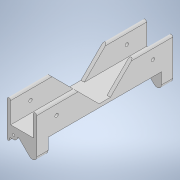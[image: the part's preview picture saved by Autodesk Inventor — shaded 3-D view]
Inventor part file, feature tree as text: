
AUTODESK INVENTOR PART (.ipt)
format: ipt  version: 2022 (Build 260153000, 153)  size: 276,480 bytes
history: native  units: mm
features: sketch x8, extrude x7, fillet x6, projected_geometry x5, plane x2, chamfer x2, mirror x1, hole x1
ambient origin geometry x8: Origin, YZ Plane, XZ Plane, XY Plane, X Axis, Y Axis, Z Axis, Center Point
bodies: Body1 (feature_tree)
feature tree (32):
  extrude  "Extrusion2"  Depth=3.0mm
  extrude  "Extrusion3"  Depth=20.0mm
  plane  "Work Plane1"
  extrude  "Extrusion4"  Depth=7.0mm
  fillet  "Fillet2"  Radius=120.0mm
  extrude  "Extrusion5"  TaperAngle=0.0deg  [1 undecoded]
  fillet  "Fillet3"  Radius=50.0mm
  fillet  "Fillet4"  Radius=1.5mm
  extrude  "Extrusion6"  Depth=3.0mm
  fillet  "Fillet6"  [1 undecoded]
  extrude  "Extrusion7"  Depth=1.0mm
  chamfer  "Chamfer1"  Distance=10.0mm
  fillet  "Fillet7"  [1 undecoded]
  plane  "Work Plane2"
  mirror  "Mirror1"
  fillet  "Fillet5"  Radius=1.5mm
  extrude  "Extrusion8"  Depth=3.75mm
  hole  "Hole1"  [1 undecoded]
  chamfer  "Chamfer2"  Distance=6.0mm
  sketch  "Sketch2"  dims[d5=3.0mm d6=3.0mm]
  sketch  "Sketch3"  dims[d7=20.0mm d8=20.0mm]
  sketch  "Sketch4"  dims[d12=7.0mm d13=7.0mm d14=120.0mm d15=0.0mm]
  projected_geometry  "Projected Loop1"
  sketch  "Sketch5"  dims[d17=2.0mm d18=0.0mm d19=0.0mm d20=50.0mm d21=0.0mm d22=1.5mm]
  projected_geometry  "Projected Loop2"
  sketch  "Sketch6"  dims[d23=2.0mm d24=3.0mm d25=0.0mm d26=0.0mm]
  sketch  "Sketch7"  dims[d27=3.5mm d28=1.0mm]
  projected_geometry  "Projected Loop3"
  sketch  "Sketch8"  dims[d29=1.0mm]
  projected_geometry  "Projected Loop4"
  sketch  "Sketch9"  dims[d30=45.0deg d31=10.0mm d32=0.0mm d33=45.0deg d34=1.5mm d35=3.75mm d36=6.0mm d37=6.0mm d38=0.0mm d39=0.5mm d40=2.0mm d41=45.0deg d42=1.0mm d43=35.0mm d44=35.0mm d45=0.0mm d46=0.0mm d47=3.0mm d48=4.5mm d49=4.0mm d50=2.0mm d51=90.0deg d52=4.5mm d53=0.0mm d54=19.999mm d55=2.0mm d56=45.0deg]
  projected_geometry  "Projected Loop5"
note: 4 required parameter values undecoded (feature->parameter linkage not recoverable at this tier; creation-order binding heuristic only, values carry confidence <= 0.55)
